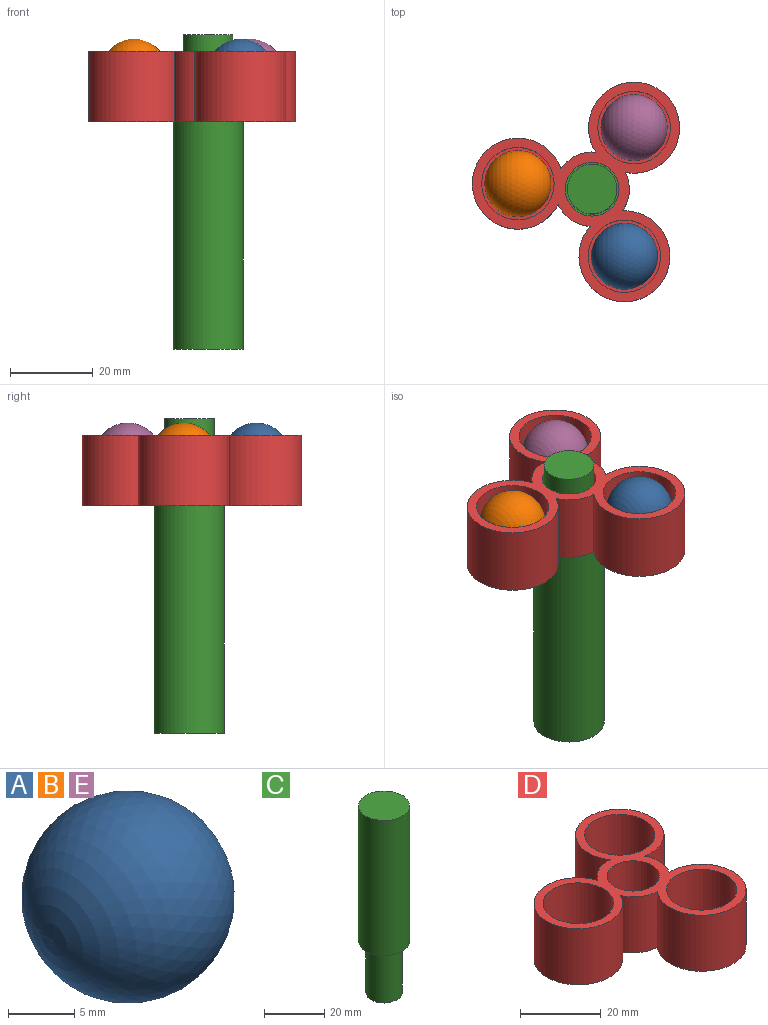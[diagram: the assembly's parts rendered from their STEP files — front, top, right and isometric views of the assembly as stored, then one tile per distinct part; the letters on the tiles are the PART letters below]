
ASSEMBLY  parts=5 mates=4
PART A: 1 faces, bbox 16x16x16 mm
  f0: sphere r=8mm, area 804.2mm2
PART B: same geometry as A
PART C: 5 faces, bbox 17x17x76 mm
  f0: cylinder r=8.5mm len=55mm, axis (0,0,-1), area 2937.4mm2, adj f1,f2
  f1: plane 17x17mm, normal (0,0,1), area 227mm2, adj f0
  f2: plane 17x17mm, normal (0,0,-1), area 113.9mm2, adj f0,f3
  f3: cylinder r=6mm len=21mm, axis (0,0,1), area 791.7mm2, adj f2,f4
  f4: plane 12x12mm, normal (0,0,-1), area 113.1mm2, adj f3
PART D: 15 faces, bbox 50.1x53.1x17 mm
  f0: cylinder r=9mm len=17mm, axis (0,0,-1), area 166.8mm2, adj f1,f7,f10,f11
  f1: cylinder r=11mm len=22mm, axis (0,0,-1), area 1023.6mm2, adj f0,f2,f10,f11
  f2: cylinder r=9mm len=17mm, axis (0,0,-1), area 166.8mm2, adj f1,f3,f10,f11
  f3: cylinder r=11mm len=22mm, axis (0,0,-1), area 1023.6mm2, adj f2,f4,f10,f11
  f4: cylinder r=9mm len=17mm, axis (0,0,-1), area 166.8mm2, adj f3,f7,f10,f11
  f5: cylinder r=8.75mm len=17.5mm, axis (0,0,-1), area 714.7mm2, adj f10,f13
  f6: cylinder r=8.75mm len=17.5mm, axis (0,0,-1), area 714.7mm2, adj f10,f14
  f7: cylinder r=11mm len=22mm, axis (0,0,-1), area 1023.6mm2, adj f0,f4,f10,f11
  f8: cylinder r=6.5mm len=17mm, axis (0,0,-1), area 694.3mm2, adj f10,f11
  f9: cylinder r=8.75mm len=17.5mm, axis (0,0,-1), area 714.7mm2, adj f10,f12
  f10: plane 53.09x50.09mm, normal (0,0,1), area 505.5mm2, adj f0,f1,f2,f3,f4,f5,f6,f7
  f11: plane 53.09x50.09mm, normal (0,0,-1), area 1227.1mm2, adj f0,f1,f2,f3,f4,f7,f8
  f12: plane 17.5x17.5mm, normal (0,0,1), area 240.5mm2, adj f9
  f13: plane 17.5x17.5mm, normal (0,0,1), area 240.5mm2, adj f5
  f14: plane 17.5x17.5mm, normal (0,0,1), area 240.5mm2, adj f6
PART E: same geometry as A
PLACE A t=(5.44,-15,12)mm
PLACE B t=(-20.33,2.56,12)mm
PLACE C rot(axis=(1,0,0),180deg) t=(-2.38,1.22,0)mm
PLACE D t=(-2.38,1.22,0)mm
PLACE E t=(7.76,16.09,12)mm
MATE fastened B.f0 <-> D.f3  axis (0,0,1) through (-20.33,2.56,12)mm
MATE fastened E.f0 <-> D.f1  axis (0,0,1) through (7.76,16.09,12)mm
MATE fastened C.f0 <-> D.f8  axis (0,0,1) through (-2.38,1.22,0)mm
MATE fastened A.f0 <-> D.f6  axis (0,0,1) through (5.44,-15,12)mm
